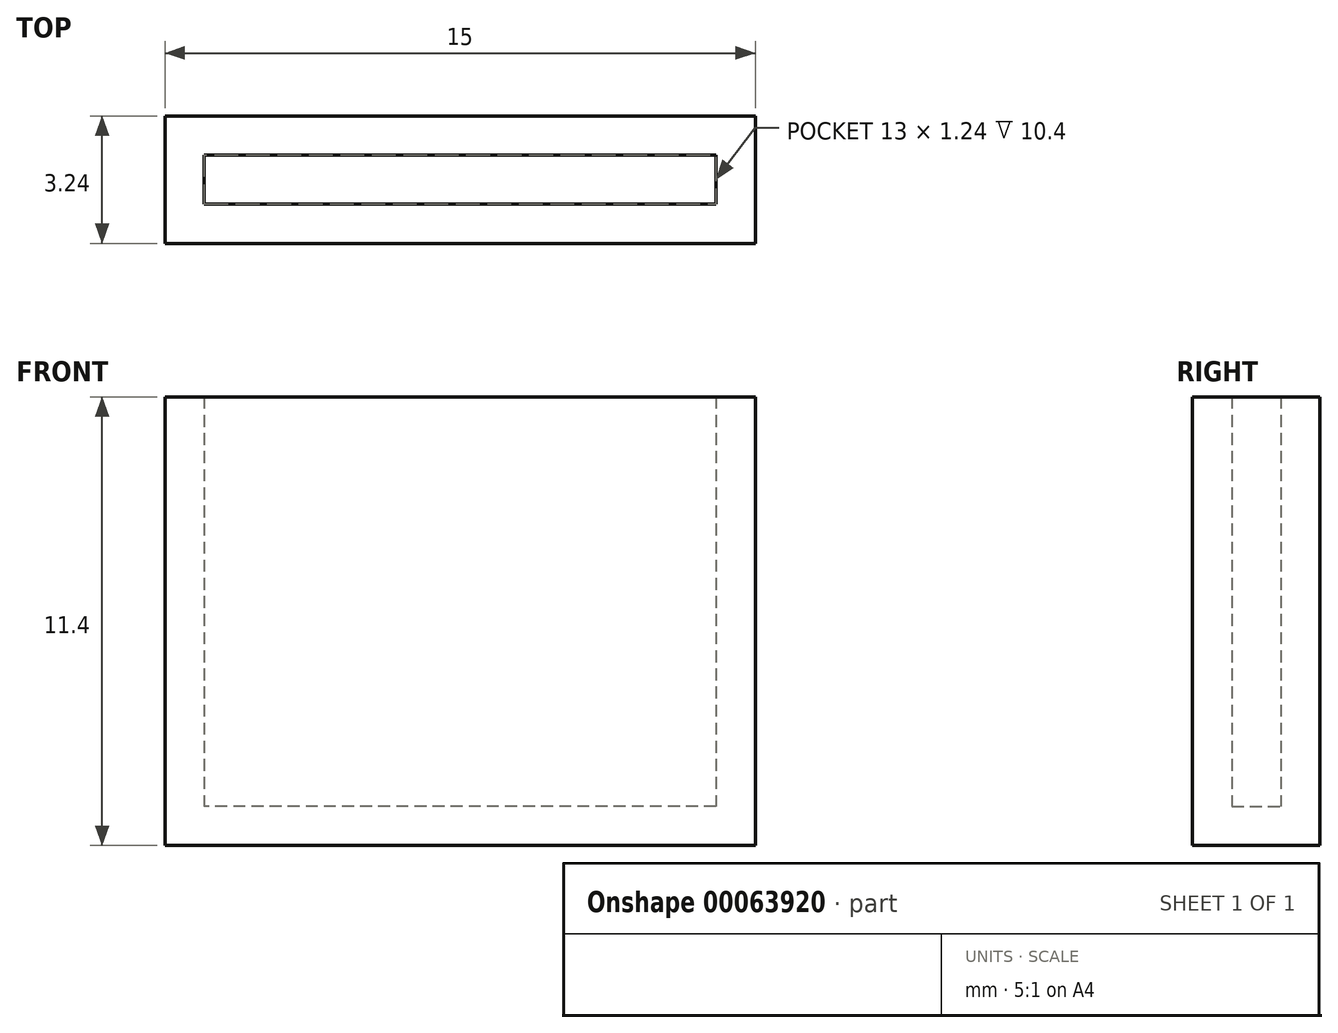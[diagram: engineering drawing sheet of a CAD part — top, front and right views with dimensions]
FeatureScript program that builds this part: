
annotation { "Feature Type Name" : "Feature", "Feature Type Description" : "" }
export const myFeature = defineFeature(function(context is Context, id is Id, definition is map)
    precondition{}
    {
        {
            assignVariable(context, id + "F0", {"name" : "wall_thickness", "anyValue" : 1});
        }
        {
            assignVariable(context, id + "F1", {"name" : "depth", "anyValue" : 5});
        }
        {
            assignVariable(context, id + "F2", {"name" : "acrylic_thickness", "anyValue" : 6.4});
        }
        {
            var Q0;
            Q0=qCreatedBy(makeId("Top.planeOp"),FACE);
            var sketch = newSketch(context, id + "F3", { "sketchPlane" : qUnion([Q0])});
            skLineSegment(sketch, "E0.bottom", {"start": v(6.5, -0.62) * mm, "end": v(-6.5, -0.62) * mm});
            skLineSegment(sketch, "E0.top", {"start": v(6.5, 0.62) * mm, "end": v(-6.5, 0.62) * mm});
            skLineSegment(sketch, "E0.left", {"start": v(6.5, -0.62) * mm, "end": v(6.5, 0.62) * mm});
            skLineSegment(sketch, "E0.right", {"start": v(-6.5, -0.62) * mm, "end": v(-6.5, 0.62) * mm});
            skPoint(sketch, "E0.middle", {"position": v(0, 0) * mm});
            skLineSegment(sketch, "E1.bottom", {"start": v(7.5, -1.62) * mm, "end": v(-7.5, -1.62) * mm});
            skLineSegment(sketch, "E1.top", {"start": v(7.5, 1.62) * mm, "end": v(-7.5, 1.62) * mm});
            skLineSegment(sketch, "E1.left", {"start": v(7.5, -1.62) * mm, "end": v(7.5, 1.62) * mm});
            skLineSegment(sketch, "E1.right", {"start": v(-7.5, -1.62) * mm, "end": v(-7.5, 1.62) * mm});
            skLineSegment(sketch, "E2.bottom", {"start": v(-6.38, 0.5) * mm, "end": v(4.38, 0.5) * mm});
            skLineSegment(sketch, "E2.top", {"start": v(-6.38, -0.5) * mm, "end": v(4.38, -0.5) * mm});
            skLineSegment(sketch, "E2.left", {"start": v(-6.38, 0.5) * mm, "end": v(-6.38, -0.5) * mm});
            skLineSegment(sketch, "E2.right", {"start": v(4.38, 0.5) * mm, "end": v(4.38, -0.5) * mm});
            skLineSegment(sketch, "E3", {"start": v(0, 0.5) * mm, "end": v(0, -0.5) * mm, "construction": true});
            skLineSegment(sketch, "E4", {"start": v(-6.5, 0) * mm, "end": v(-6.38, 0) * mm, "construction": true});
            skSolve(sketch);
        }
        {
            var Q0;
            Q0=makeQuery(id+"F3.imprint","IMPRINT",FACE,{"disambiguationData":[TD([[makeQuery(id+"F3.imprint","IMPRINT",EDGE,{"derivedFrom":sQuery(id+"F3.wireOp",EDGE,"E0.bottom")}),1.0]])]});
            extrude(context, id + "F4", {"entities" : qUnion([Q0]), "depth" : (getVariable(context, 'depth') + getVariable(context, 'acrylic_thickness')) * mm});
        }
        {
            var Q0;
            Q0=makeQuery(id+"F3.imprint","IMPRINT",FACE,{"disambiguationData":[TD([[makeQuery(id+"F3.imprint","IMPRINT",EDGE,{"derivedFrom":sQuery(id+"F3.wireOp",EDGE,"E0.bottom")}),-1.0]])]});
            var Q1;
            Q1=makeQuery(id+"F3.imprint","IMPRINT",FACE,{"disambiguationData":[TD([[makeQuery(id+"F3.imprint","IMPRINT",EDGE,{"derivedFrom":sQuery(id+"F3.wireOp",EDGE,"E2.bottom")}),-1.0]])]});
            extrude(context, id + "F5", {"entities" : qUnion([Q0, Q1]), "operationType" : NewBodyOperationType.ADD, "depth" : (getVariable(context, 'wall_thickness')) * mm});
        }
    });
